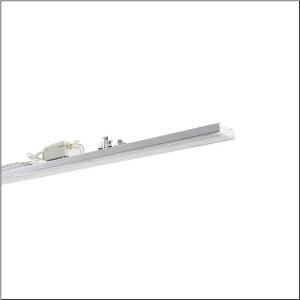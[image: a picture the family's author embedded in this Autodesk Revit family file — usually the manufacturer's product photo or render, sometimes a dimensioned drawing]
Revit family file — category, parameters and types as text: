
# Revit family: licross_21_recessed_mo_52tl12de45xg
name_source: partatom
category: Lighting Fixtures
units: mm (PartAtom-declared; Revit-internal decimal feet)

## family parameters
Cut with Voids When Loaded = No
Host = Face
Light Source = No
Part Type = Normal
Room Calculation Point = No
Round Connector Dimension = Use Diameter
Shared = No

## types (1)
- --- (1 x LED, 5140 lm, 29.9 W, 4000K)
    Apparent Load = 30 VA
    CIE Flux Codes = 72 92 99 100 100
    Color Rendering = 80
    Color Temperature = 4000K
    Default Elevation = 1800 mm
    Description = Licross 21 Recessed MO, luminaire insert, of sheet steel, galvanised, coil coated, white, length: 750mm, width: 66mm, height: 67mm, LED rated luminous flux: 5.140lm, light colour: 840, SDCM (Standard Deviation of Colour Matching)MacAdam ≤ 3 SDCM (initial), control gear: DALI 2, with plug, 5-pole, with phase selection, mains connection: 220..240V, AC, 50/60Hz, rated input power: 30W, internal wiring halogen-free, primary light control with lens, of plastic, primary optical cover: cover, of PMMA, light emission: direct distribution, primary light characteristic: symmetric, protection rating (complete): IP40, insulation class (complete): insulation class I (protective earthing), certification: CE, ENEC, VDE, UKCA, protection symbol: D if used in an environment without relevant dust loads with corresponding accessories, impact resistance: IK06, permissible ambient temperature for indoor applications: -25..+35°C, corresponds to IFS (International Featured Standards) requirements for safety and quality in the food industry, reducing of maximum allowable ambient temperature of 5°C with ceiling mounting, LABS conformity tested according to VDMA 24364:2018-05, The light source and the operating device comply with the requirements of the Ecodesign Regulation (EU) 2019/2020 and are replaceable in accordance with this regulation, packaging unit: 1 piece
    Height = 58 mm
    Lamp = 1 x LED
    Lamp Light Flux = 5140 lm
    Lamp Power = 29.9 W
    Lamp count = 1
    Length = 750 mm
    Luminous efficacy = 172 lm/W
    Manufacturer = Siteco
    ModVariant = No
    Model = 52TL12DE45XG
    Mounting Place = Ceiling
    Mounting Type = Pendant
    Number of Poles = 1
    OnlyDefault = Yes
    Power Factor = 1
    Product Name = Licross 21 Recessed MO
    Product group = luminaire insert | ceiling pendant
    ProductGroupID = 901
    Protection Class = Protection class I
    Protection Degree = IP 40
    RLX_Detail_Level = 1
    RLX_Emergency_Light_Flux = 0 lm
    RLX_Emergency_Type = 0
    RLX_Emergency_Type_DB = No
    RlxData = <blob elided: 29325 chars, md5=4cc142a1>
    Socket = socket
    Standby Power = 0 W
    System Light Flux = 5140 lm
    System Power = 30 W
    Type Comments = factory setting: luminous flux: 100 % | dim-lin: 254 | 390 mA
    Type Image = l_1296930.jpg
    URL = http://relux.com
    VarID = @adj_128261
    Voltage = 0 V
    Weight = 0.00 kg
    Width = 66 mm

## geometry (parser evidence)
native form markers: Blend x4, Sweep x9
no freeform markers — native parametric forms only
